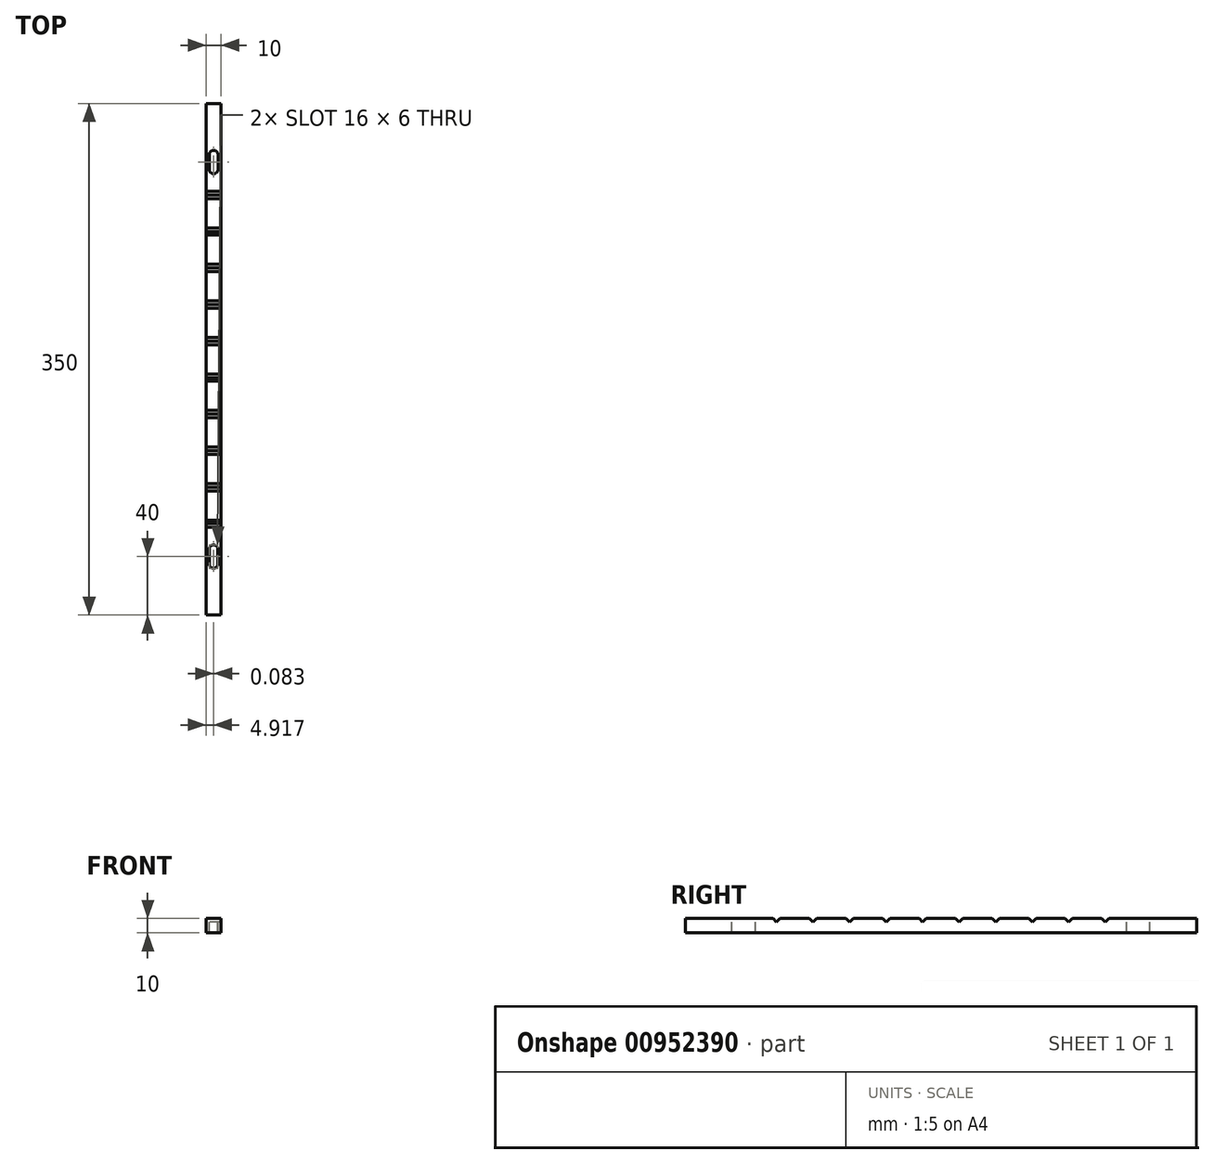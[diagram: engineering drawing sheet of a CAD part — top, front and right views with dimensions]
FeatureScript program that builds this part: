
annotation { "Feature Type Name" : "Feature", "Feature Type Description" : "" }
export const myFeature = defineFeature(function(context is Context, id is Id, definition is map)
    precondition{}
    {
        {
            var Q0;
            Q0=qCreatedBy(makeId("Front.planeOp"),FACE);
            var sketch = newSketch(context, id + "F0", { "sketchPlane" : qUnion([Q0])});
            skLineSegment(sketch, "E0.bottom", {"start": v(0, 0) * mm, "end": v(10, 0) * mm});
            skLineSegment(sketch, "E0.top", {"start": v(0, 10) * mm, "end": v(10, 10) * mm});
            skLineSegment(sketch, "E0.left", {"start": v(0, 0) * mm, "end": v(0, 10) * mm});
            skLineSegment(sketch, "E0.right", {"start": v(10, 0) * mm, "end": v(10, 10) * mm});
            skSolve(sketch);
        }
        {
            var Q0;
            Q0=makeQuery(id+"F0.imprint","IMPRINT",FACE,{"disambiguationData":[TD([[makeQuery(id+"F0.imprint","IMPRINT",EDGE,{"derivedFrom":sQuery(id+"F0.wireOp",EDGE,"E0.bottom")}),1.0]])]});
            extrude(context, id + "F1", {"entities" : qUnion([Q0]), "depth" : 350 * mm, "offsetDistance" : 25 * mm});
        }
        {
            var Q0;
            Q0=makeQuery(id+"F1.opExtrude","SWEPT_FACE",FACE,{"disambiguationData":[OSD([sQuery(id+"F0.wireOp",EDGE,"E0.left")])]});
            var sketch = newSketch(context, id + "F2", { "sketchPlane" : qUnion([Q0])});
            skLineSegment(sketch, "E1", {"start": v(65, 10) * mm, "end": v(60, 10) * mm});
            skLineSegment(sketch, "E2", {"start": v(60, 10) * mm, "end": v(62.5, 7.5) * mm});
            skLineSegment(sketch, "E3", {"start": v(62.5, 7.5) * mm, "end": v(65, 10) * mm});
            skLineSegment(sketch, "E4.1.0.0", {"start": v(90, 10) * mm, "end": v(85, 10) * mm});
            skLineSegment(sketch, "E4.1.0.1", {"start": v(85, 10) * mm, "end": v(87.5, 7.5) * mm});
            skLineSegment(sketch, "E4.1.0.2", {"start": v(87.5, 7.5) * mm, "end": v(90, 10) * mm});
            skLineSegment(sketch, "E4.2.0.0", {"start": v(115, 10) * mm, "end": v(110, 10) * mm});
            skLineSegment(sketch, "E4.2.0.1", {"start": v(110, 10) * mm, "end": v(112.5, 7.5) * mm});
            skLineSegment(sketch, "E4.2.0.2", {"start": v(112.5, 7.5) * mm, "end": v(115, 10) * mm});
            skLineSegment(sketch, "E4.3.0.0", {"start": v(140, 10) * mm, "end": v(135, 10) * mm});
            skLineSegment(sketch, "E4.3.0.1", {"start": v(135, 10) * mm, "end": v(137.5, 7.5) * mm});
            skLineSegment(sketch, "E4.3.0.2", {"start": v(137.5, 7.5) * mm, "end": v(140, 10) * mm});
            skLineSegment(sketch, "E4.4.0.0", {"start": v(165, 10) * mm, "end": v(160, 10) * mm});
            skLineSegment(sketch, "E4.4.0.1", {"start": v(160, 10) * mm, "end": v(162.5, 7.5) * mm});
            skLineSegment(sketch, "E4.4.0.2", {"start": v(162.5, 7.5) * mm, "end": v(165, 10) * mm});
            skLineSegment(sketch, "E4.5.0.0", {"start": v(190, 10) * mm, "end": v(185, 10) * mm});
            skLineSegment(sketch, "E4.5.0.1", {"start": v(185, 10) * mm, "end": v(187.5, 7.5) * mm});
            skLineSegment(sketch, "E4.5.0.2", {"start": v(187.5, 7.5) * mm, "end": v(190, 10) * mm});
            skLineSegment(sketch, "E4.6.0.0", {"start": v(215, 10) * mm, "end": v(210, 10) * mm});
            skLineSegment(sketch, "E4.6.0.1", {"start": v(210, 10) * mm, "end": v(212.5, 7.5) * mm});
            skLineSegment(sketch, "E4.6.0.2", {"start": v(212.5, 7.5) * mm, "end": v(215, 10) * mm});
            skLineSegment(sketch, "E4.7.0.0", {"start": v(240, 10) * mm, "end": v(235, 10) * mm});
            skLineSegment(sketch, "E4.7.0.1", {"start": v(235, 10) * mm, "end": v(237.5, 7.5) * mm});
            skLineSegment(sketch, "E4.7.0.2", {"start": v(237.5, 7.5) * mm, "end": v(240, 10) * mm});
            skLineSegment(sketch, "E4.8.0.0", {"start": v(265, 10) * mm, "end": v(260, 10) * mm});
            skLineSegment(sketch, "E4.8.0.1", {"start": v(260, 10) * mm, "end": v(262.5, 7.5) * mm});
            skLineSegment(sketch, "E4.8.0.2", {"start": v(262.5, 7.5) * mm, "end": v(265, 10) * mm});
            skLineSegment(sketch, "E4.9.0.0", {"start": v(290, 10) * mm, "end": v(285, 10) * mm});
            skLineSegment(sketch, "E4.9.0.1", {"start": v(285, 10) * mm, "end": v(287.5, 7.5) * mm});
            skLineSegment(sketch, "E4.9.0.2", {"start": v(287.5, 7.5) * mm, "end": v(290, 10) * mm});
            skLineSegment(sketch, "E4.direction1", {"start": v(60, 10) * mm, "end": v(85, 10) * mm, "construction": true});
            skSolve(sketch);
        }
        {
            var Q0;
            Q0 = qSketchRegion(id + "F2", true);
            extrude(context, id + "F3", {"entities" : qUnion([Q0]), "operationType" : NewBodyOperationType.REMOVE, "oppositeDirection" : true, "depth" : 25 * mm, "offsetDistance" : 25 * mm});
        }
        {
            var Q0;
            {var subQ2=sQuery(id+"F0.wireOp",EDGE,"E0.top");Q0=makeQuery(id+"F3.boolean.opBoolean","SPLIT",FACE,{"disambiguationData":[TD([makeQuery(id+"F3.opExtrude","SWEPT_FACE",FACE,{"disambiguationData":[OSD([sQuery(id+"F2.wireOp",EDGE,"E2")])]})])],"derivedFrom":makeQuery(id+"F1.opExtrude","SWEPT_FACE",FACE,{"disambiguationData":[OSD([subQ2])]})});}
            var sketch = newSketch(context, id + "F4", { "sketchPlane" : qUnion([Q0])});
            skPoint(sketch, "E5", {"position": v(5, -40) * mm});
            skPoint(sketch, "E5.positionSnap0", {"position": v(5, 0) * mm});
            skPoint(sketch, "E6", {"position": v(5, -310) * mm});
            skArc(sketch, "E7", {"start": v(8, -35) * mm, "mid": v(5, -32) * mm, "end": v(2, -35) * mm});
            skLineSegment(sketch, "E8", {"start": v(8, -35) * mm, "end": v(8, -45) * mm});
            skLineSegment(sketch, "E9", {"start": v(2, -45) * mm, "end": v(2, -35) * mm});
            skArc(sketch, "E10.MirrorCS", {"start": v(8, -45) * mm, "mid": v(5, -48) * mm, "end": v(2, -45) * mm});
            skArc(sketch, "E11", {"start": v(7.92, -305) * mm, "mid": v(4.92, -302) * mm, "end": v(1.92, -305) * mm});
            skLineSegment(sketch, "E12", {"start": v(7.92, -305) * mm, "end": v(7.92, -315) * mm});
            skLineSegment(sketch, "E13", {"start": v(1.92, -315) * mm, "end": v(1.92, -305) * mm});
            skArc(sketch, "E14.MirrorCS", {"start": v(7.92, -315) * mm, "mid": v(4.92, -318) * mm, "end": v(1.92, -315) * mm});
            skSolve(sketch);
        }
        {
            var Q0;
            Q0 = qSketchRegion(id + "F4", true);
            extrude(context, id + "F5", {"entities" : qUnion([Q0]), "operationType" : NewBodyOperationType.REMOVE, "endBound" : BoundingType.THROUGH_ALL, "oppositeDirection" : true, "depth" : 25 * mm, "offsetDistance" : 25 * mm});
        }
    });
